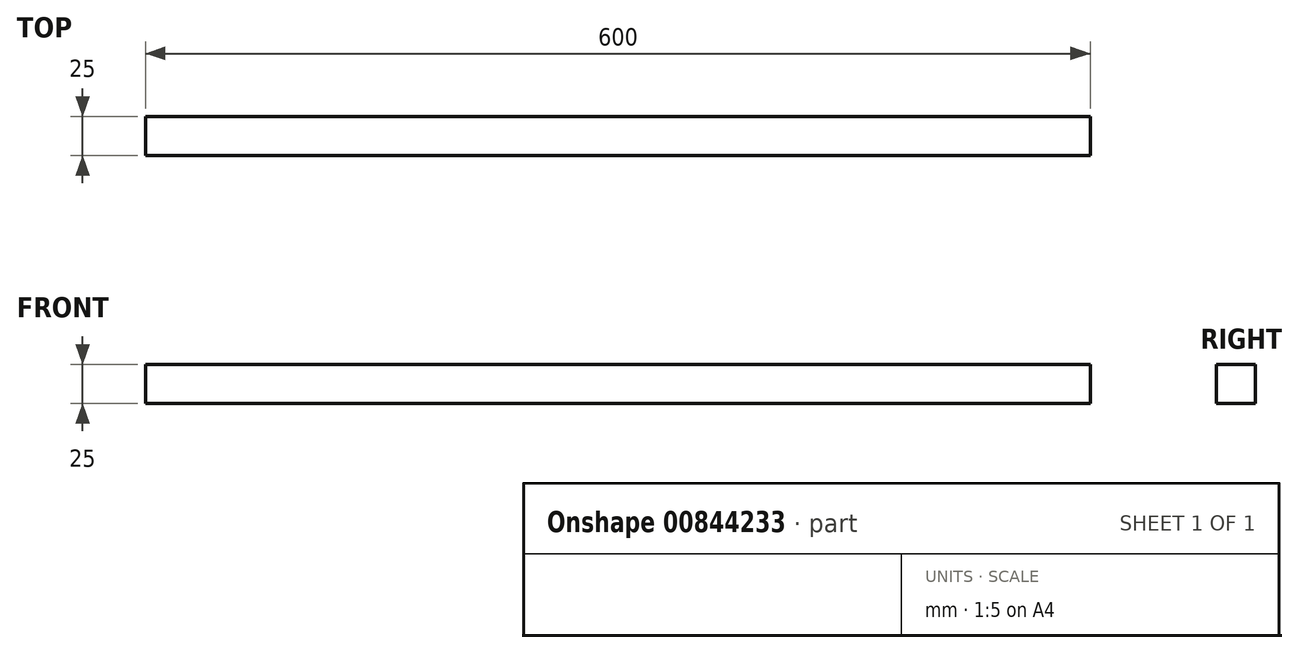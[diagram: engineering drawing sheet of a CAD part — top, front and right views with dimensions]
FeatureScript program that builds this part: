
annotation { "Feature Type Name" : "Feature", "Feature Type Description" : "" }
export const myFeature = defineFeature(function(context is Context, id is Id, definition is map)
    precondition{}
    {
        {
            var Q0;
            Q0=qCreatedBy(makeId("Right.planeOp"),FACE);
            var sketch = newSketch(context, id + "F0", { "sketchPlane" : qUnion([Q0])});
            skLineSegment(sketch, "E0.bottom", {"start": v(0, 0) * mm, "end": v(-43.34, 0) * mm});
            skLineSegment(sketch, "E0.top", {"start": v(0, 30.72) * mm, "end": v(-43.34, 30.72) * mm});
            skLineSegment(sketch, "E0.left", {"start": v(0, 0) * mm, "end": v(0, 30.72) * mm});
            skLineSegment(sketch, "E0.right", {"start": v(-43.34, 0) * mm, "end": v(-43.34, 30.72) * mm});
            skSolve(sketch);
        }
        {
            var Q0;
            Q0=makeQuery(id+"F0.imprint","IMPRINT",FACE,{"disambiguationData":[TD([[makeQuery(id+"F0.imprint","IMPRINT",EDGE,{"derivedFrom":sQuery(id+"F0.wireOp",EDGE,"E0.bottom")}),-1.0]])]});
            extrude(context, id + "F1", {"entities" : qUnion([Q0]), "depth" : 600 * mm, "offsetDistance" : 25 * mm});
        }
        {
            var Q0;
            Q0=makeQuery(id+"F1.opExtrude","SWEPT_FACE",FACE,{"disambiguationData":[OSD([sQuery(id+"F0.wireOp",EDGE,"E0.left")])]});
            extrude(context, id + "F2", {"entities" : qUnion([Q0]), "operationType" : NewBodyOperationType.INTERSECT, "oppositeDirection" : true, "depth" : 25 * mm, "offsetDistance" : 25 * mm});
        }
        {
            var Q0;
            Q0=makeQuery(id+"F1.opExtrude","SWEPT_FACE",FACE,{"disambiguationData":[OSD([sQuery(id+"F0.wireOp",EDGE,"E0.bottom")])]});
            extrude(context, id + "F3", {"entities" : qUnion([Q0]), "operationType" : NewBodyOperationType.INTERSECT, "oppositeDirection" : true, "depth" : 25 * mm, "offsetDistance" : 25 * mm});
        }
    });
